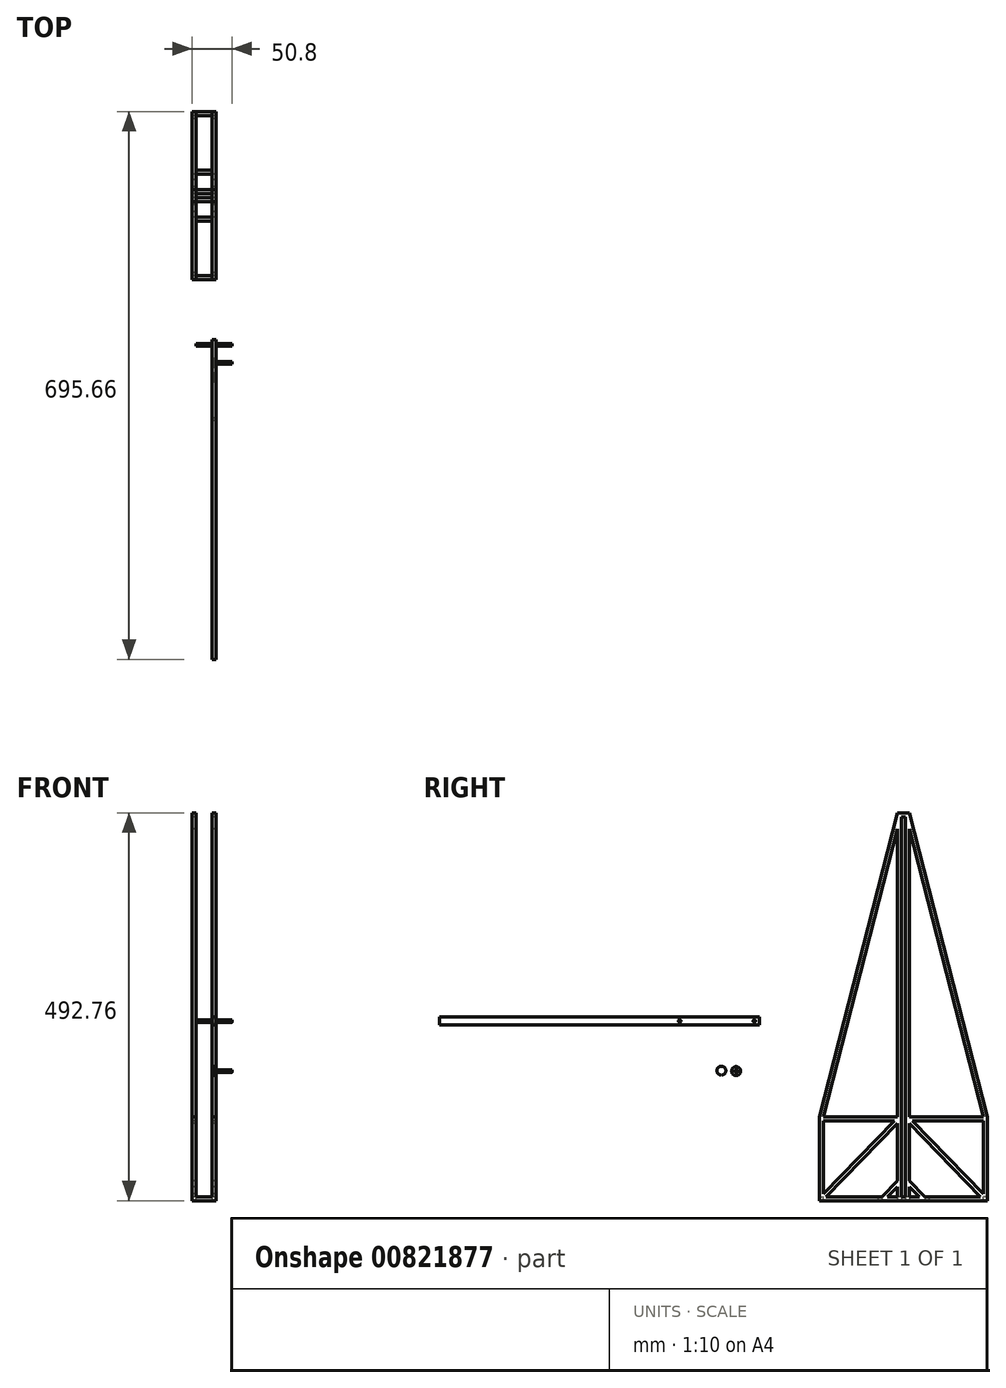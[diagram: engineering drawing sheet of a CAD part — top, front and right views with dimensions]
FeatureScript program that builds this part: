
annotation { "Feature Type Name" : "Feature", "Feature Type Description" : "" }
export const myFeature = defineFeature(function(context is Context, id is Id, definition is map)
    precondition{}
    {
        {
            var Q0;
            Q0=qCreatedBy(makeId("Right.planeOp"),FACE);
            var sketch = newSketch(context, id + "F0", { "sketchPlane" : qUnion([Q0])});
            skLineSegment(sketch, "E0.bottom", {"start": v(0, 0) * mm, "end": v(101.6, 0) * mm});
            skLineSegment(sketch, "E0.top", {"start": v(0, -101.6) * mm, "end": v(101.6, -101.6) * mm});
            skLineSegment(sketch, "E0.left", {"start": v(0, 0) * mm, "end": v(0, -101.6) * mm});
            skLineSegment(sketch, "E0.right", {"start": v(101.6, 0) * mm, "end": v(101.6, -101.6) * mm});
            skLineSegment(sketch, "E1.bottom", {"start": v(0, 0) * mm, "end": v(-101.6, 0) * mm});
            skLineSegment(sketch, "E1.top", {"start": v(0, -101.6) * mm, "end": v(-101.6, -101.6) * mm});
            skLineSegment(sketch, "E1.right", {"start": v(-101.6, 0) * mm, "end": v(-101.6, -101.6) * mm});
            skLineSegment(sketch, "E2.0", {"start": v(106.68, 0) * mm, "end": v(106.68, -106.68) * mm});
            skLineSegment(sketch, "E2.1", {"start": v(0, -106.68) * mm, "end": v(106.68, -106.68) * mm});
            skLineSegment(sketch, "E2.2", {"start": v(0, -106.68) * mm, "end": v(-106.68, -106.68) * mm});
            skLineSegment(sketch, "E2.3", {"start": v(-106.68, 0) * mm, "end": v(-106.68, -106.68) * mm});
            skLineSegment(sketch, "E3.0", {"start": v(0, -5.08) * mm, "end": v(101.6, -5.08) * mm});
            skLineSegment(sketch, "E3.1", {"start": v(0, -5.08) * mm, "end": v(-101.6, -5.08) * mm});
            skLineSegment(sketch, "E4", {"start": v(-106.68, 0) * mm, "end": v(-101.6, 0) * mm});
            skLineSegment(sketch, "E5", {"start": v(101.6, 0) * mm, "end": v(106.68, 0) * mm});
            skLineSegment(sketch, "E6.0", {"start": v(2.54, 0) * mm, "end": v(2.54, 381) * mm});
            skLineSegment(sketch, "E7.0", {"start": v(-2.54, 0) * mm, "end": v(-2.54, 381) * mm});
            skLineSegment(sketch, "E8", {"start": v(-2.54, 381) * mm, "end": v(2.54, 381) * mm});
            skLineSegment(sketch, "E9", {"start": v(2.54, 381) * mm, "end": v(7.62, 381) * mm});
            skLineSegment(sketch, "E10", {"start": v(7.62, 381) * mm, "end": v(7.62, 0) * mm});
            skLineSegment(sketch, "E11.0", {"start": v(-7.62, 0) * mm, "end": v(-7.62, 381) * mm});
            skLineSegment(sketch, "E12", {"start": v(-7.62, 381) * mm, "end": v(-2.54, 381) * mm});
            skLineSegment(sketch, "E13", {"start": v(-7.62, 381) * mm, "end": v(-7.62, 386.08) * mm});
            skLineSegment(sketch, "E14", {"start": v(-7.62, 386.08) * mm, "end": v(7.62, 386.08) * mm});
            skLineSegment(sketch, "E15", {"start": v(7.62, 386.08) * mm, "end": v(7.62, 381) * mm});
            skLineSegment(sketch, "E16", {"start": v(-2.54, 0) * mm, "end": v(-2.54, -101.6) * mm});
            skLineSegment(sketch, "E17", {"start": v(-7.62, 0) * mm, "end": v(-7.62, -101.6) * mm});
            skLineSegment(sketch, "E18", {"start": v(2.54, 0) * mm, "end": v(2.54, -101.6) * mm});
            skLineSegment(sketch, "E19", {"start": v(7.62, 0) * mm, "end": v(7.62, -101.6) * mm});
            skLineSegment(sketch, "E20", {"start": v(-7.62, -101.6) * mm, "end": v(-7.62, -88.9) * mm});
            skLineSegment(sketch, "E21", {"start": v(-7.62, -101.6) * mm, "end": v(-20.32, -101.6) * mm});
            skLineSegment(sketch, "E22", {"start": v(-20.32, -101.6) * mm, "end": v(-7.62, -88.9) * mm});
            skLineSegment(sketch, "E23.0", {"start": v(-23.91, -98) * mm, "end": v(-11.21, -85.3) * mm});
            skLineSegment(sketch, "E24", {"start": v(-23.91, -98) * mm, "end": v(-27.5, -101.6) * mm});
            skLineSegment(sketch, "E25", {"start": v(-11.21, -85.3) * mm, "end": v(-7.62, -81.72) * mm});
            skLineSegment(sketch, "E26.MirrorCS", {"start": v(23.91, -98) * mm, "end": v(27.5, -101.6) * mm});
            skLineSegment(sketch, "E27.MirrorCS", {"start": v(23.91, -98) * mm, "end": v(11.21, -85.3) * mm});
            skLineSegment(sketch, "E28.MirrorCS", {"start": v(20.32, -101.6) * mm, "end": v(7.62, -88.9) * mm});
            skLineSegment(sketch, "E29.MirrorCS", {"start": v(11.21, -85.3) * mm, "end": v(7.62, -81.72) * mm});
            skLineSegment(sketch, "E30", {"start": v(-7.62, 386.08) * mm, "end": v(-106.68, 0) * mm});
            skPoint(sketch, "E31", {"position": v(-7.62, 365.64) * mm});
            skPoint(sketch, "E32", {"position": v(-101.44, 0) * mm});
            skLineSegment(sketch, "E33", {"start": v(-101.44, 0) * mm, "end": v(-7.62, 365.64) * mm});
            skLineSegment(sketch, "E34.MirrorCS", {"start": v(101.44, 0) * mm, "end": v(7.62, 365.64) * mm});
            skLineSegment(sketch, "E35.MirrorCS", {"start": v(7.62, 386.08) * mm, "end": v(106.68, 0) * mm});
            skPoint(sketch, "E36", {"position": v(-101.6, -97.96) * mm});
            skPoint(sketch, "E37", {"position": v(-98.05, -101.6) * mm});
            skPoint(sketch, "E38", {"position": v(-7.62, -8.72) * mm});
            skPoint(sketch, "E39", {"position": v(-11.17, -5.08) * mm});
            skLineSegment(sketch, "E40", {"start": v(-7.62, -8.72) * mm, "end": v(-98.05, -101.6) * mm});
            skLineSegment(sketch, "E41", {"start": v(-101.6, -97.96) * mm, "end": v(-11.17, -5.08) * mm});
            skLineSegment(sketch, "E42.MirrorCS", {"start": v(101.6, -97.96) * mm, "end": v(11.17, -5.08) * mm});
            skLineSegment(sketch, "E43.MirrorCS", {"start": v(7.62, -8.72) * mm, "end": v(98.05, -101.6) * mm});
            skSolve(sketch);
        }
        {
            var Q0;
            Q0=makeQuery(id+"F0.imprint","IMPRINT",FACE,{"disambiguationData":[TD([[makeQuery(id+"F0.imprint","IMPRINT",EDGE,{"derivedFrom":sQuery(id+"F0.wireOp",EDGE,"E2.0")}),-1.0]])]});
            var Q1;
            {var subQ0=sQuery(id+"F0.wireOp",EDGE,"E3.0");var subQ1=sQuery(id+"F0.wireOp",EDGE,"E0.right");var subQ2=makeQuery(id+"F0.imprint","INTERSECT",VERTEX,{"derivedFrom":[subQ1,subQ0]});Q1=makeQuery(id+"F0.imprint","IMPRINT",FACE,{"disambiguationData":[TD([[makeQuery(id+"F0.imprint","IMPRINT",EDGE,{"disambiguationData":[TD([[subQ2,1.0]])],"derivedFrom":subQ0}),1.0]])]});}
            var Q2;
            {var subQ0=sQuery(id+"F0.wireOp",EDGE,"E3.1");var subQ1=sQuery(id+"F0.wireOp",EDGE,"E1.right");var subQ2=makeQuery(id+"F0.imprint","INTERSECT",VERTEX,{"derivedFrom":[subQ1,subQ0]});Q2=makeQuery(id+"F0.imprint","IMPRINT",FACE,{"disambiguationData":[TD([[makeQuery(id+"F0.imprint","IMPRINT",EDGE,{"disambiguationData":[TD([[subQ2,1.0]])],"derivedFrom":subQ0}),-1.0]])]});}
            var Q3;
            {var subQ4=sQuery(id+"F0.wireOp",EDGE,"E6.0");Q3=makeQuery(id+"F0.imprint","IMPRINT",FACE,{"disambiguationData":[TD([[makeQuery(id+"F0.imprint","IMPRINT",EDGE,{"derivedFrom":subQ4}),-1.0]])]});}
            var Q4;
            {var subQ5=sQuery(id+"F0.wireOp",EDGE,"E7.0");Q4=makeQuery(id+"F0.imprint","IMPRINT",FACE,{"disambiguationData":[TD([[makeQuery(id+"F0.imprint","IMPRINT",EDGE,{"derivedFrom":subQ5}),1.0]])]});}
            var Q5;
            Q5=makeQuery(id+"F0.imprint","IMPRINT",FACE,{"disambiguationData":[TD([[makeQuery(id+"F0.imprint","IMPRINT",EDGE,{"derivedFrom":sQuery(id+"F0.wireOp",EDGE,"E8")}),1.0]])]});
            var Q6;
            {var subQ3=sQuery(id+"F0.wireOp",EDGE,"E16");var subQ4=sQuery(id+"F0.wireOp",EDGE,"E1.top");var subQ5=makeQuery(id+"F0.imprint","INTERSECT",VERTEX,{"derivedFrom":[subQ4,subQ3]});Q6=makeQuery(id+"F0.imprint","IMPRINT",FACE,{"disambiguationData":[TD([[makeQuery(id+"F0.imprint","IMPRINT",EDGE,{"disambiguationData":[TD([[subQ5,-1.0]])],"derivedFrom":subQ4}),-1.0]])]});}
            var Q7;
            {var subQ0=sQuery(id+"F0.wireOp",EDGE,"E40");Q7=makeQuery(id+"F0.imprint","IMPRINT",FACE,{"disambiguationData":[TD([[makeQuery(id+"F0.imprint","IMPRINT",EDGE,{"derivedFrom":subQ0}),-1.0]])]});}
            var Q8;
            {var subQ3=sQuery(id+"F0.wireOp",EDGE,"E18");var subQ5=sQuery(id+"F0.wireOp",EDGE,"E3.0");var subQ7=makeQuery(id+"F0.imprint","INTERSECT",VERTEX,{"derivedFrom":[subQ5,subQ3]});Q8=makeQuery(id+"F0.imprint","IMPRINT",FACE,{"disambiguationData":[TD([[makeQuery(id+"F0.imprint","IMPRINT",EDGE,{"disambiguationData":[TD([[subQ7,-1.0]])],"derivedFrom":subQ5}),1.0]])]});}
            var Q9;
            {var subQ3=sQuery(id+"F0.wireOp",EDGE,"E16");var subQ5=sQuery(id+"F0.wireOp",EDGE,"E3.1");var subQ6=makeQuery(id+"F0.imprint","INTERSECT",VERTEX,{"derivedFrom":[subQ5,subQ3]});Q9=makeQuery(id+"F0.imprint","IMPRINT",FACE,{"disambiguationData":[TD([[makeQuery(id+"F0.imprint","IMPRINT",EDGE,{"disambiguationData":[TD([[subQ6,-1.0]])],"derivedFrom":subQ5}),-1.0]])]});}
            var Q10;
            {var subQ0=sQuery(id+"F0.wireOp",EDGE,"E18");var subQ1=sQuery(id+"F0.wireOp",EDGE,"E0.top");var subQ2=makeQuery(id+"F0.imprint","INTERSECT",VERTEX,{"derivedFrom":[subQ1,subQ0]});Q10=makeQuery(id+"F0.imprint","IMPRINT",FACE,{"disambiguationData":[TD([[makeQuery(id+"F0.imprint","IMPRINT",EDGE,{"disambiguationData":[TD([[subQ2,-1.0]])],"derivedFrom":subQ1}),1.0]])]});}
            var Q11;
            {var subQ4=sQuery(id+"F0.wireOp",EDGE,"E42.MirrorCS");Q11=makeQuery(id+"F0.imprint","IMPRINT",FACE,{"disambiguationData":[TD([[makeQuery(id+"F0.imprint","IMPRINT",EDGE,{"derivedFrom":subQ4}),1.0]])]});}
            var Q12;
            {var subQ0=sQuery(id+"F0.wireOp",EDGE,"E26.MirrorCS");Q12=makeQuery(id+"F0.imprint","IMPRINT",FACE,{"disambiguationData":[TD([[makeQuery(id+"F0.imprint","IMPRINT",EDGE,{"derivedFrom":subQ0}),-1.0]])]});}
            var Q13;
            {var subQ0=sQuery(id+"F0.wireOp",EDGE,"E22");Q13=makeQuery(id+"F0.imprint","IMPRINT",FACE,{"disambiguationData":[TD([[makeQuery(id+"F0.imprint","IMPRINT",EDGE,{"derivedFrom":subQ0}),1.0]])]});}
            var Q14;
            {var subQ3=sQuery(id+"F0.wireOp",EDGE,"E5");Q14=makeQuery(id+"F0.imprint","IMPRINT",FACE,{"disambiguationData":[TD([[makeQuery(id+"F0.imprint","IMPRINT",EDGE,{"derivedFrom":subQ3}),1.0]])]});}
            var Q15;
            {var subQ1=sQuery(id+"F0.wireOp",EDGE,"E4");Q15=makeQuery(id+"F0.imprint","IMPRINT",FACE,{"disambiguationData":[TD([[makeQuery(id+"F0.imprint","IMPRINT",EDGE,{"derivedFrom":subQ1}),1.0]])]});}
            extrude(context, id + "F1", {"entities" : qUnion([Q0, Q1, Q2, Q3, Q4, Q5, Q6, Q7, Q8, Q9, Q10, Q11, Q12, Q13, Q14, Q15]), "depth" : 5.08 * mm, "offsetDistance" : 25.4 * mm});
        }
        {
            var Q0;
            Q0=makeQuery(id+"F1.opExtrude","SWEPT_BODY",BODY,{"disambiguationData":[OSD([sQuery(id+"F0.wireOp",EDGE,"E0.bottom"),sQuery(id+"F0.wireOp",EDGE,"E0.top"),sQuery(id+"F0.wireOp",EDGE,"E0.right"),sQuery(id+"F0.wireOp",EDGE,"E1.bottom"),sQuery(id+"F0.wireOp",EDGE,"E1.top"),sQuery(id+"F0.wireOp",EDGE,"E1.right"),sQuery(id+"F0.wireOp",EDGE,"E2.0"),sQuery(id+"F0.wireOp",EDGE,"E2.1"),sQuery(id+"F0.wireOp",EDGE,"E2.2"),sQuery(id+"F0.wireOp",EDGE,"E2.3"),sQuery(id+"F0.wireOp",EDGE,"E3.0"),sQuery(id+"F0.wireOp",EDGE,"E3.1"),sQuery(id+"F0.wireOp",EDGE,"E6.0"),sQuery(id+"F0.wireOp",EDGE,"E7.0"),sQuery(id+"F0.wireOp",EDGE,"E8"),sQuery(id+"F0.wireOp",EDGE,"E10"),sQuery(id+"F0.wireOp",EDGE,"E11.0"),sQuery(id+"F0.wireOp",EDGE,"E14"),sQuery(id+"F0.wireOp",EDGE,"E16"),sQuery(id+"F0.wireOp",EDGE,"E17"),sQuery(id+"F0.wireOp",EDGE,"E18"),sQuery(id+"F0.wireOp",EDGE,"E19"),sQuery(id+"F0.wireOp",EDGE,"E22"),sQuery(id+"F0.wireOp",EDGE,"E23.0"),sQuery(id+"F0.wireOp",EDGE,"E24"),sQuery(id+"F0.wireOp",EDGE,"E25"),sQuery(id+"F0.wireOp",EDGE,"E26.MirrorCS"),sQuery(id+"F0.wireOp",EDGE,"E27.MirrorCS"),sQuery(id+"F0.wireOp",EDGE,"E28.MirrorCS"),sQuery(id+"F0.wireOp",EDGE,"E29.MirrorCS"),sQuery(id+"F0.wireOp",EDGE,"E30"),sQuery(id+"F0.wireOp",EDGE,"E33"),sQuery(id+"F0.wireOp",EDGE,"E34.MirrorCS"),sQuery(id+"F0.wireOp",EDGE,"E35.MirrorCS"),sQuery(id+"F0.wireOp",EDGE,"E40"),sQuery(id+"F0.wireOp",EDGE,"E41"),sQuery(id+"F0.wireOp",EDGE,"E42.MirrorCS"),sQuery(id+"F0.wireOp",EDGE,"E43.MirrorCS")])]});
            transform(context, id + "F2", {"entities" : qUnion([Q0]), "transformType" : TransformType.COPY});
        }
        {
            var Q0;
            Q0=makeQuery(id+"F2.opPattern","COPY",BODY,{"derivedFrom":makeQuery(id+"F1.opExtrude","SWEPT_BODY",BODY,{"disambiguationData":[OSD([sQuery(id+"F0.wireOp",EDGE,"E0.bottom"),sQuery(id+"F0.wireOp",EDGE,"E0.top"),sQuery(id+"F0.wireOp",EDGE,"E0.right"),sQuery(id+"F0.wireOp",EDGE,"E1.bottom"),sQuery(id+"F0.wireOp",EDGE,"E1.top"),sQuery(id+"F0.wireOp",EDGE,"E1.right"),sQuery(id+"F0.wireOp",EDGE,"E2.0"),sQuery(id+"F0.wireOp",EDGE,"E2.1"),sQuery(id+"F0.wireOp",EDGE,"E2.2"),sQuery(id+"F0.wireOp",EDGE,"E2.3"),sQuery(id+"F0.wireOp",EDGE,"E3.0"),sQuery(id+"F0.wireOp",EDGE,"E3.1"),sQuery(id+"F0.wireOp",EDGE,"E6.0"),sQuery(id+"F0.wireOp",EDGE,"E7.0"),sQuery(id+"F0.wireOp",EDGE,"E8"),sQuery(id+"F0.wireOp",EDGE,"E10"),sQuery(id+"F0.wireOp",EDGE,"E11.0"),sQuery(id+"F0.wireOp",EDGE,"E14"),sQuery(id+"F0.wireOp",EDGE,"E16"),sQuery(id+"F0.wireOp",EDGE,"E17"),sQuery(id+"F0.wireOp",EDGE,"E18"),sQuery(id+"F0.wireOp",EDGE,"E19"),sQuery(id+"F0.wireOp",EDGE,"E22"),sQuery(id+"F0.wireOp",EDGE,"E23.0"),sQuery(id+"F0.wireOp",EDGE,"E24"),sQuery(id+"F0.wireOp",EDGE,"E25"),sQuery(id+"F0.wireOp",EDGE,"E26.MirrorCS"),sQuery(id+"F0.wireOp",EDGE,"E27.MirrorCS"),sQuery(id+"F0.wireOp",EDGE,"E28.MirrorCS"),sQuery(id+"F0.wireOp",EDGE,"E29.MirrorCS"),sQuery(id+"F0.wireOp",EDGE,"E30"),sQuery(id+"F0.wireOp",EDGE,"E33"),sQuery(id+"F0.wireOp",EDGE,"E34.MirrorCS"),sQuery(id+"F0.wireOp",EDGE,"E35.MirrorCS"),sQuery(id+"F0.wireOp",EDGE,"E40"),sQuery(id+"F0.wireOp",EDGE,"E41"),sQuery(id+"F0.wireOp",EDGE,"E42.MirrorCS"),sQuery(id+"F0.wireOp",EDGE,"E43.MirrorCS")])]}),"instanceName":"1"});
            transform(context, id + "F3", {"entities" : qUnion([Q0]), "transformType" : TransformType.TRANSLATION_3D, "dx" : -25.4 * mm, "dy" : 0 * mm, "dz" : 0 * mm, "makeCopy" : false});
        }
        {
            var Q0;
            Q0=makeQuery(id+"F1.opExtrude","CAP_FACE",FACE,{"disambiguationData":[OSD([sQuery(id+"F0.wireOp",EDGE,"E0.bottom"),sQuery(id+"F0.wireOp",EDGE,"E0.top"),sQuery(id+"F0.wireOp",EDGE,"E0.right"),sQuery(id+"F0.wireOp",EDGE,"E1.bottom"),sQuery(id+"F0.wireOp",EDGE,"E1.top"),sQuery(id+"F0.wireOp",EDGE,"E1.right"),sQuery(id+"F0.wireOp",EDGE,"E2.0"),sQuery(id+"F0.wireOp",EDGE,"E2.1"),sQuery(id+"F0.wireOp",EDGE,"E2.2"),sQuery(id+"F0.wireOp",EDGE,"E2.3"),sQuery(id+"F0.wireOp",EDGE,"E3.0"),sQuery(id+"F0.wireOp",EDGE,"E3.1"),sQuery(id+"F0.wireOp",EDGE,"E6.0"),sQuery(id+"F0.wireOp",EDGE,"E7.0"),sQuery(id+"F0.wireOp",EDGE,"E8"),sQuery(id+"F0.wireOp",EDGE,"E10"),sQuery(id+"F0.wireOp",EDGE,"E11.0"),sQuery(id+"F0.wireOp",EDGE,"E14"),sQuery(id+"F0.wireOp",EDGE,"E16"),sQuery(id+"F0.wireOp",EDGE,"E17"),sQuery(id+"F0.wireOp",EDGE,"E18"),sQuery(id+"F0.wireOp",EDGE,"E19"),sQuery(id+"F0.wireOp",EDGE,"E22"),sQuery(id+"F0.wireOp",EDGE,"E23.0"),sQuery(id+"F0.wireOp",EDGE,"E24"),sQuery(id+"F0.wireOp",EDGE,"E25"),sQuery(id+"F0.wireOp",EDGE,"E26.MirrorCS"),sQuery(id+"F0.wireOp",EDGE,"E27.MirrorCS"),sQuery(id+"F0.wireOp",EDGE,"E28.MirrorCS"),sQuery(id+"F0.wireOp",EDGE,"E29.MirrorCS"),sQuery(id+"F0.wireOp",EDGE,"E30"),sQuery(id+"F0.wireOp",EDGE,"E33"),sQuery(id+"F0.wireOp",EDGE,"E34.MirrorCS"),sQuery(id+"F0.wireOp",EDGE,"E35.MirrorCS"),sQuery(id+"F0.wireOp",EDGE,"E40"),sQuery(id+"F0.wireOp",EDGE,"E41"),sQuery(id+"F0.wireOp",EDGE,"E42.MirrorCS"),sQuery(id+"F0.wireOp",EDGE,"E43.MirrorCS")])],"isStart":true});
            var sketch = newSketch(context, id + "F4", { "sketchPlane" : qUnion([Q0])});
            skLineSegment(sketch, "E44.bottom", {"start": v(-106.68, -106.68) * mm, "end": v(-101.6, -106.68) * mm});
            skLineSegment(sketch, "E44.top", {"start": v(-106.68, -101.6) * mm, "end": v(-101.6, -101.6) * mm});
            skLineSegment(sketch, "E44.left", {"start": v(-106.68, -106.68) * mm, "end": v(-106.68, -101.6) * mm});
            skLineSegment(sketch, "E44.right", {"start": v(-101.6, -106.68) * mm, "end": v(-101.6, -101.6) * mm});
            skLineSegment(sketch, "E45.bottom", {"start": v(106.68, -106.68) * mm, "end": v(101.6, -106.68) * mm});
            skLineSegment(sketch, "E45.top", {"start": v(106.68, -101.6) * mm, "end": v(101.6, -101.6) * mm});
            skLineSegment(sketch, "E45.left", {"start": v(106.68, -106.68) * mm, "end": v(106.68, -101.6) * mm});
            skLineSegment(sketch, "E45.right", {"start": v(101.6, -106.68) * mm, "end": v(101.6, -101.6) * mm});
            skLineSegment(sketch, "E46.bottom", {"start": v(-7.62, -101.6) * mm, "end": v(-2.54, -101.6) * mm});
            skLineSegment(sketch, "E46.top", {"start": v(-7.62, -106.68) * mm, "end": v(-2.54, -106.68) * mm});
            skLineSegment(sketch, "E46.left", {"start": v(-7.62, -101.6) * mm, "end": v(-7.62, -106.68) * mm});
            skLineSegment(sketch, "E46.right", {"start": v(-2.54, -101.6) * mm, "end": v(-2.54, -106.68) * mm});
            skLineSegment(sketch, "E47.bottom", {"start": v(2.54, -101.6) * mm, "end": v(7.62, -101.6) * mm});
            skLineSegment(sketch, "E47.top", {"start": v(2.54, -106.68) * mm, "end": v(7.62, -106.68) * mm});
            skLineSegment(sketch, "E47.left", {"start": v(2.54, -101.6) * mm, "end": v(2.54, -106.68) * mm});
            skLineSegment(sketch, "E47.right", {"start": v(7.62, -101.6) * mm, "end": v(7.62, -106.68) * mm});
            skLineSegment(sketch, "E48.bottom", {"start": v(27.5, -101.6) * mm, "end": v(32.58, -101.6) * mm});
            skLineSegment(sketch, "E48.top", {"start": v(27.5, -106.68) * mm, "end": v(32.58, -106.68) * mm});
            skLineSegment(sketch, "E48.left", {"start": v(27.5, -101.6) * mm, "end": v(27.5, -106.68) * mm});
            skLineSegment(sketch, "E48.right", {"start": v(32.58, -101.6) * mm, "end": v(32.58, -106.68) * mm});
            skLineSegment(sketch, "E49.bottom", {"start": v(-27.5, -101.6) * mm, "end": v(-32.58, -101.6) * mm});
            skLineSegment(sketch, "E49.top", {"start": v(-27.5, -106.68) * mm, "end": v(-32.58, -106.68) * mm});
            skLineSegment(sketch, "E49.left", {"start": v(-27.5, -101.6) * mm, "end": v(-27.5, -106.68) * mm});
            skLineSegment(sketch, "E49.right", {"start": v(-32.58, -101.6) * mm, "end": v(-32.58, -106.68) * mm});
            skSolve(sketch);
        }
        {
            var Q0;
            Q0=makeQuery(id+"F4.imprint","IMPRINT",FACE,{"disambiguationData":[TD([[makeQuery(id+"F4.imprint","IMPRINT",EDGE,{"derivedFrom":sQuery(id+"F4.wireOp",EDGE,"E44.bottom")}),1.0]])]});
            var Q1;
            Q1=makeQuery(id+"F4.imprint","IMPRINT",FACE,{"disambiguationData":[TD([[makeQuery(id+"F4.imprint","IMPRINT",EDGE,{"derivedFrom":sQuery(id+"F4.wireOp",EDGE,"E49.bottom")}),1.0]])]});
            var Q2;
            Q2=makeQuery(id+"F4.imprint","IMPRINT",FACE,{"disambiguationData":[TD([[makeQuery(id+"F4.imprint","IMPRINT",EDGE,{"derivedFrom":sQuery(id+"F4.wireOp",EDGE,"E46.bottom")}),-1.0]])]});
            var Q3;
            Q3=makeQuery(id+"F4.imprint","IMPRINT",FACE,{"disambiguationData":[TD([[makeQuery(id+"F4.imprint","IMPRINT",EDGE,{"derivedFrom":sQuery(id+"F4.wireOp",EDGE,"E47.bottom")}),-1.0]])]});
            var Q4;
            Q4=makeQuery(id+"F4.imprint","IMPRINT",FACE,{"disambiguationData":[TD([[makeQuery(id+"F4.imprint","IMPRINT",EDGE,{"derivedFrom":sQuery(id+"F4.wireOp",EDGE,"E48.bottom")}),-1.0]])]});
            var Q5;
            Q5=makeQuery(id+"F4.imprint","IMPRINT",FACE,{"disambiguationData":[TD([[makeQuery(id+"F4.imprint","IMPRINT",EDGE,{"derivedFrom":sQuery(id+"F4.wireOp",EDGE,"E45.bottom")}),1.0]])]});
            extrude(context, id + "F5", {"entities" : qUnion([Q0, Q1, Q2, Q3, Q4, Q5]), "operationType" : NewBodyOperationType.ADD, "endBound" : BoundingType.UP_TO_NEXT, "depth" : 25.4 * mm, "offsetDistance" : 25.4 * mm});
        }
        {
            var Q0;
            Q0=qCreatedBy(makeId("Right.planeOp"),FACE);
            var sketch = newSketch(context, id + "F6", { "sketchPlane" : qUnion([Q0])});
            skLineSegment(sketch, "E50.bottom", {"start": v(-182.58, 126.66) * mm, "end": v(-588.98, 126.66) * mm});
            skLineSegment(sketch, "E50.top", {"start": v(-182.58, 116.5) * mm, "end": v(-588.98, 116.5) * mm});
            skLineSegment(sketch, "E50.left", {"start": v(-182.58, 126.66) * mm, "end": v(-182.58, 116.5) * mm});
            skLineSegment(sketch, "E50.right", {"start": v(-588.98, 126.66) * mm, "end": v(-588.98, 116.5) * mm});
            skCircle(sketch, "E51", {"center": v(-284.18, 121.58) * mm, "radius": 1.59 * mm});
            skLineSegment(sketch, "E52", {"start": v(-187.66, 121.58) * mm, "end": v(-190.84, 121.58) * mm});
            skCircle(sketch, "E53", {"center": v(-189.25, 121.58) * mm, "radius": 1.59 * mm});
            skSolve(sketch);
        }
        {
            var Q0;
            Q0=makeQuery(id+"F6.imprint","IMPRINT",FACE,{"disambiguationData":[TD([[makeQuery(id+"F6.imprint","IMPRINT",EDGE,{"derivedFrom":sQuery(id+"F6.wireOp",EDGE,"E50.bottom")}),1.0]])]});
            var Q1;
            {var subQ0=sQuery(id+"F6.wireOp",EDGE,"E52");Q1=makeQuery(id+"F6.imprint","IMPRINT",FACE,{"disambiguationData":[TD([[makeQuery(id+"F6.imprint","IMPRINT",EDGE,{"derivedFrom":subQ0}),1.0]])]});}
            var Q2;
            {var subQ0=sQuery(id+"F6.wireOp",EDGE,"E52");Q2=makeQuery(id+"F6.imprint","IMPRINT",FACE,{"disambiguationData":[TD([[makeQuery(id+"F6.imprint","IMPRINT",EDGE,{"derivedFrom":subQ0}),-1.0]])]});}
            extrude(context, id + "F7", {"entities" : qUnion([Q0, Q1, Q2]), "depth" : 5.08 * mm, "offsetDistance" : 25.4 * mm});
        }
        {
            var Q0;
            Q0=qCreatedBy(makeId("Right.planeOp"),FACE);
            var sketch = newSketch(context, id + "F8", { "sketchPlane" : qUnion([Q0])});
            skCircle(sketch, "E54", {"center": v(-212.43, 57.86) * mm, "radius": 5.72 * mm});
            skCircle(sketch, "E55", {"center": v(-212.43, 57.86) * mm, "radius": 1.59 * mm});
            skSolve(sketch);
        }
        {
            var Q0;
            Q0=makeQuery(id+"F8.imprint","IMPRINT",FACE,{"disambiguationData":[TD([[makeQuery(id+"F8.imprint","IMPRINT",EDGE,{"derivedFrom":sQuery(id+"F8.wireOp",EDGE,"E54")}),1.0]])]});
            var Q1;
            Q1=makeQuery(id+"F8.imprint","IMPRINT",FACE,{"disambiguationData":[TD([[makeQuery(id+"F8.imprint","IMPRINT",EDGE,{"derivedFrom":sQuery(id+"F8.wireOp",EDGE,"E55")}),1.0]])]});
            extrude(context, id + "F9", {"entities" : qUnion([Q0, Q1]), "depth" : 2.54 * mm, "offsetDistance" : 25.4 * mm});
        }
        {
            var Q0;
            Q0=makeQuery(id+"F8.imprint","IMPRINT",FACE,{"disambiguationData":[TD([[makeQuery(id+"F8.imprint","IMPRINT",EDGE,{"derivedFrom":sQuery(id+"F8.wireOp",EDGE,"E55")}),1.0]])]});
            extrude(context, id + "F10", {"entities" : qUnion([Q0]), "operationType" : NewBodyOperationType.ADD, "depth" : 25.4 * mm, "offsetDistance" : 25.4 * mm});
        }
        {
            var Q0;
            Q0=qCreatedBy(makeId("Right.planeOp"),FACE);
            var sketch = newSketch(context, id + "F11", { "sketchPlane" : qUnion([Q0])});
            skCircle(sketch, "E56", {"center": v(-231.2, 58.48) * mm, "radius": 5.72 * mm});
            skSolve(sketch);
        }
        {
            var Q0;
            Q0=makeQuery(id+"F11.imprint","IMPRINT",FACE,{"disambiguationData":[TD([[makeQuery(id+"F11.imprint","IMPRINT",EDGE,{"derivedFrom":sQuery(id+"F11.wireOp",EDGE,"E56")}),1.0]])]});
            extrude(context, id + "F12", {"entities" : qUnion([Q0]), "depth" : 2.54 * mm, "offsetDistance" : 25.4 * mm});
        }
        {
            var Q0;
            Q0=qCreatedBy(makeId("Right.planeOp"),FACE);
            var sketch = newSketch(context, id + "F13", { "sketchPlane" : qUnion([Q0])});
            skCircle(sketch, "E57", {"center": v(-173.65, 60.41) * mm, "radius": 1.59 * mm});
            skSolve(sketch);
        }
        {
            var Q0;
            Q0=sQuery(id+"F13.wireOp",EDGE,"E57");
            extrude(context, id + "F14", {"bodyType" : ToolBodyType.SURFACE, "surfaceEntities" : qUnion([Q0]), "depth" : 40.64 * mm, "offsetDistance" : 25.4 * mm});
        }
        {
            var Q0;
            {var subQ0=sQuery(id+"F6.wireOp",EDGE,"E52");Q0=makeQuery(id+"F6.imprint","IMPRINT",FACE,{"disambiguationData":[TD([[makeQuery(id+"F6.imprint","IMPRINT",EDGE,{"derivedFrom":subQ0}),-1.0]])]});}
            var Q1;
            {var subQ0=sQuery(id+"F6.wireOp",EDGE,"E52");Q1=makeQuery(id+"F6.imprint","IMPRINT",FACE,{"disambiguationData":[TD([[makeQuery(id+"F6.imprint","IMPRINT",EDGE,{"derivedFrom":subQ0}),1.0]])]});}
            extrude(context, id + "F15", {"entities" : qUnion([Q0, Q1]), "operationType" : NewBodyOperationType.ADD, "depth" : 25.4 * mm, "offsetDistance" : 25.4 * mm});
        }
        {
            var Q0;
            {var subQ0=sQuery(id+"F6.wireOp",EDGE,"E52");Q0=makeQuery(id+"F6.imprint","IMPRINT",FACE,{"disambiguationData":[TD([[makeQuery(id+"F6.imprint","IMPRINT",EDGE,{"derivedFrom":subQ0}),-1.0]])]});}
            var Q1;
            {var subQ0=sQuery(id+"F6.wireOp",EDGE,"E52");Q1=makeQuery(id+"F6.imprint","IMPRINT",FACE,{"disambiguationData":[TD([[makeQuery(id+"F6.imprint","IMPRINT",EDGE,{"derivedFrom":subQ0}),1.0]])]});}
            extrude(context, id + "F16", {"entities" : qUnion([Q0, Q1]), "operationType" : NewBodyOperationType.ADD, "oppositeDirection" : true, "depth" : 20.32 * mm, "offsetDistance" : 25.4 * mm});
        }
    });
